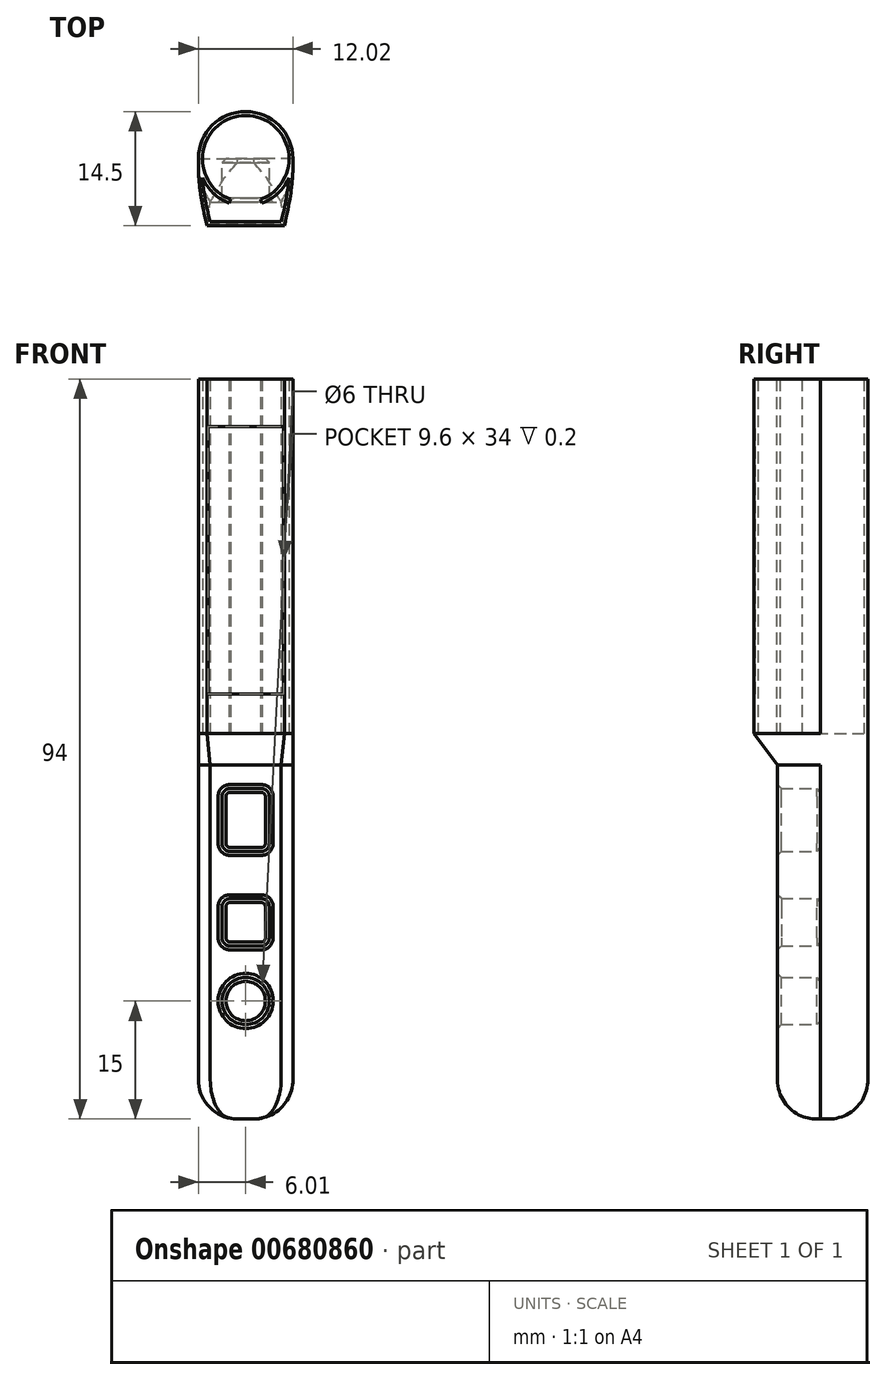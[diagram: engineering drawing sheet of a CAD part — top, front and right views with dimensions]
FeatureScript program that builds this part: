
annotation { "Feature Type Name" : "Feature", "Feature Type Description" : "" }
export const myFeature = defineFeature(function(context is Context, id is Id, definition is map)
    precondition{}
    {
        {
            var Q0;
            Q0=qCreatedBy(makeId("Top.planeOp"),FACE);
            var sketch = newSketch(context, id + "F0", { "sketchPlane" : qUnion([Q0])});
            skArc(sketch, "E0", {"start": v(1.91, -5.16) * mm, "mid": v(5.41, 0.97) * mm, "end": v(0, 5.5) * mm});
            skLineSegment(sketch, "E1.bottom", {"start": v(-5.5, 0) * mm, "end": v(5.5, 0) * mm});
            skLineSegment(sketch, "E1.top", {"start": v(-4.5, -8) * mm, "end": v(4.5, -8) * mm});
            skLineSegment(sketch, "E2.bottom", {"start": v(-6, 0) * mm, "end": v(6, 0) * mm});
            skLineSegment(sketch, "E2.top", {"start": v(-4.91, -8.5) * mm, "end": v(4.91, -8.5) * mm});
            skLineSegment(sketch, "E3.right", {"start": v(-2.09, -5.62) * mm, "end": v(-1.91, -5.16) * mm});
            skPoint(sketch, "E3.middle", {"position": v(0, -6) * mm});
            skArc(sketch, "E4.trimOffspring", {"start": v(-5.5, -2.4) * mm, "mid": v(-4.12, -4.36) * mm, "end": v(-2.09, -5.62) * mm});
            skArc(sketch, "E5.trimOffspring", {"start": v(6, 0) * mm, "mid": v(0, 6) * mm, "end": v(-6, 0) * mm});
            skLineSegment(sketch, "E6", {"start": v(4.5, -8) * mm, "end": v(-4.5, -8) * mm});
            skFitSpline(sketch, "E7", {"points": [v(-6, 0) * mm, v(-4.91, -8.5) * mm], "startDerivative": vector(-0.16, -5.74) * mm, "endDerivative": vector(3.03, -12.46) * mm});
            skFitSpline(sketch, "E8", {"points": [v(-5.5, -2.4) * mm, v(-4.5, -8) * mm], "startDerivative": vector(0.65, -6.73) * mm, "endDerivative": vector(1.57, -6.04) * mm});
            skPoint(sketch, "E9.MirrorCS.end.orphan", {"position": v(4.91, -8.5) * mm});
            skPoint(sketch, "E9.MirrorCS.start.orphan", {"position": v(6, 0) * mm});
            skPoint(sketch, "E10.MirrorCS.end.orphan", {"position": v(4.5, -8) * mm});
            skPoint(sketch, "E10.MirrorCS.start.orphan", {"position": v(5.5, -2.4) * mm});
            skFitSpline(sketch, "E11.MirrorCS", {"points": [v(6, 0) * mm, v(4.91, -8.5) * mm], "startDerivative": vector(0.16, -5.74) * mm, "endDerivative": vector(-3.03, -12.46) * mm});
            skFitSpline(sketch, "E12.MirrorCS", {"points": [v(5.5, -2.4) * mm, v(4.5, -8) * mm], "startDerivative": vector(-0.65, -6.73) * mm, "endDerivative": vector(-1.57, -6.04) * mm});
            skArc(sketch, "E13.MirrorCS", {"start": v(5.5, -2.4) * mm, "mid": v(4.12, -4.36) * mm, "end": v(2.09, -5.62) * mm});
            skLineSegment(sketch, "E14.MirrorCS", {"start": v(2.09, -5.62) * mm, "end": v(1.91, -5.16) * mm});
            skArc(sketch, "E15", {"start": v(0, 5.5) * mm, "mid": v(-5.41, 0.97) * mm, "end": v(-1.91, -5.16) * mm});
            skSolve(sketch);
        }
        {
            var Q0;
            Q0 = qSketchRegion(id + "F0", true);
            extrude(context, id + "F1", {"entities" : qUnion([Q0]), "depth" : 45 * mm, "offsetDistance" : 25.4 * mm});
        }
        {
            var Q0;
            Q0=makeQuery(id+"F1.opExtrude","SWEPT_FACE",FACE,{"disambiguationData":[OSD([sQuery(id+"F0.wireOp",EDGE,"E2.top")])]});
            var sketch = newSketch(context, id + "F2", { "sketchPlane" : qUnion([Q0])});
            skLineSegment(sketch, "E16.bottom", {"start": v(-4.91, 5) * mm, "end": v(4.8, 5) * mm});
            skLineSegment(sketch, "E16.top", {"start": v(-4.8, 39) * mm, "end": v(4.91, 39) * mm});
            skLineSegment(sketch, "E16.left", {"start": v(-4.8, 5) * mm, "end": v(-4.8, 39) * mm});
            skLineSegment(sketch, "E16.right", {"start": v(4.8, 5) * mm, "end": v(4.8, 39) * mm});
            skPoint(sketch, "E16.middle", {"position": v(0, 22) * mm});
            skSolve(sketch);
        }
        {
            var Q0;
            Q0=qCreatedBy(makeId("Top.planeOp"),FACE);
            cPlane(context, id + "F3", {"entities" : qUnion([Q0]), "cplaneType" : CPlaneType.OFFSET, "offset" : 4 * mm, "oppositeDirection" : true, "width" : 150 * mm, "height" : 150 * mm});
        }
        {
            var Q0;
            {var subQ2=sQuery(id+"F2.wireOp",EDGE,"E16.left");Q0=makeQuery(id+"F2.imprint","IMPRINT",FACE,{"disambiguationData":[TD([[makeQuery(id+"F2.imprint","IMPRINT",EDGE,{"derivedFrom":subQ2}),-1.0]])]});}
            extrude(context, id + "F4", {"entities" : qUnion([Q0]), "operationType" : NewBodyOperationType.REMOVE, "depth" : -0.2 * mm, "offsetDistance" : 25 * mm});
        }
        {
            var Q0;
            Q0=qCreatedBy(makeId("Top.planeOp"),FACE);
            var sketch = newSketch(context, id + "F5", { "sketchPlane" : qUnion([Q0])});
            skArc(sketch, "E17", {"start": v(6, 0) * mm, "mid": v(0, 6) * mm, "end": v(-6, 0) * mm});
            skLineSegment(sketch, "E18", {"start": v(-4.91, -8.5) * mm, "end": v(4.91, -8.5) * mm});
            skFitSpline(sketch, "E19", {"points": [v(-6, 0) * mm, v(-4.91, -8.5) * mm], "startDerivative": vector(0.05, -13.63) * mm, "endDerivative": vector(1.73, -8.34) * mm});
            skFitSpline(sketch, "E20.MirrorCS", {"points": [v(6, 0) * mm, v(4.91, -8.5) * mm], "startDerivative": vector(-0.05, -13.63) * mm, "endDerivative": vector(-1.73, -8.34) * mm});
            skSolve(sketch);
        }
        {
            var Q0;
            Q0=qCreatedBy(id+"F3.planeOp",FACE);
            var sketch = newSketch(context, id + "F6", { "sketchPlane" : qUnion([Q0])});
            skArc(sketch, "E21", {"start": v(6, 0) * mm, "mid": v(0, 6) * mm, "end": v(-6, 0) * mm});
            skLineSegment(sketch, "E22", {"start": v(-4.5, -5.5) * mm, "end": v(4.5, -5.5) * mm});
            skFitSpline(sketch, "E23", {"points": [v(-6, 0) * mm, v(-4.5, -5.5) * mm], "startDerivative": vector(-0.15, -9.4) * mm, "endDerivative": vector(2.63, -4.6) * mm});
            skFitSpline(sketch, "E24.MirrorCS", {"points": [v(6, 0) * mm, v(4.5, -5.5) * mm], "startDerivative": vector(0.15, -9.4) * mm, "endDerivative": vector(-2.63, -4.6) * mm});
            skPoint(sketch, "E25", {"position": v(0, -5.5) * mm});
            skSolve(sketch);
        }
        {
            var Q0;
            Q0=qCreatedBy(makeId("Right.planeOp"),FACE);
            var sketch = newSketch(context, id + "F7", { "sketchPlane" : qUnion([Q0])});
            skFitSpline(sketch, "E26", {"points": [v(-8.5, 0) * mm, v(-5.5, -4) * mm], "startDerivative": vector(-0.11, -4.2) * mm, "endDerivative": vector(0.02, -5.23) * mm});
            skLineSegment(sketch, "E27", {"start": v(6, 0) * mm, "end": v(6, -4) * mm});
            skSolve(sketch);
        }
        {
            var Q1;
            Q1=makeQuery(id+"F5.imprint","IMPRINT",FACE,{"disambiguationData":[TD([[makeQuery(id+"F5.imprint","IMPRINT",EDGE,{"derivedFrom":sQuery(id+"F5.wireOp",EDGE,"E17")}),1.0]])]});
            var Q2;
            Q2=makeQuery(id+"F6.imprint","IMPRINT",FACE,{"disambiguationData":[TD([[makeQuery(id+"F6.imprint","IMPRINT",EDGE,{"derivedFrom":sQuery(id+"F6.wireOp",EDGE,"E21")}),1.0]])]});
            var Q3;
            Q3=sQuery(id+"F7.wireOp",EDGE,"E26");
            loft(context, id + "F8", {"operationType" : NewBodyOperationType.ADD, "sheetProfilesArray" : [{ "sheetProfileEntities" : qUnion([Q1]) }, { "sheetProfileEntities" : qUnion([Q2]) }], "guidesArray" : [{ "guideEntities" : qUnion([Q3]), "guideDerivativeType" : LoftGuideDerivativeType.DEFAULT, "guideDerivativeMagnitude" : 1 }]});
        }
        {
            var Q0;
            Q0=makeQuery(id+"F6.imprint","IMPRINT",FACE,{"disambiguationData":[TD([[makeQuery(id+"F6.imprint","IMPRINT",EDGE,{"derivedFrom":sQuery(id+"F6.wireOp",EDGE,"E21")}),1.0]])]});
            extrude(context, id + "F9", {"entities" : qUnion([Q0]), "operationType" : NewBodyOperationType.ADD, "oppositeDirection" : true, "depth" : 45 * mm, "offsetDistance" : 25 * mm});
        }
        {
            var Q0;
            Q0=makeQuery(id+"F9.opExtrude","CAP_FACE",FACE,{"disambiguationData":[OSD([sQuery(id+"F6.wireOp",EDGE,"E21"),sQuery(id+"F6.wireOp",EDGE,"E22"),sQuery(id+"F6.wireOp",EDGE,"E23"),sQuery(id+"F6.wireOp",EDGE,"E24.MirrorCS")])],"isStart":false});
            fillet(context, id + "F10", {"entities" : qUnion([Q0]), "radius" : 5 * mm, "tangentPropagation" : true, "allowEdgeOverflow" : false});
        }
        {
            var Q0;
            Q0=qCreatedBy(makeId("Front.planeOp"),FACE);
            var sketch = newSketch(context, id + "F11", { "sketchPlane" : qUnion([Q0])});
            skLineSegment(sketch, "E28.bottom", {"start": v(-2, -7) * mm, "end": v(2, -7) * mm});
            skLineSegment(sketch, "E28.top", {"start": v(-2, -15) * mm, "end": v(2, -15) * mm});
            skLineSegment(sketch, "E28.left", {"start": v(-3, -8) * mm, "end": v(-3, -14) * mm});
            skLineSegment(sketch, "E28.right", {"start": v(3, -8) * mm, "end": v(3, -14) * mm});
            skLineSegment(sketch, "E29.bottom", {"start": v(-2, -21) * mm, "end": v(2, -21) * mm});
            skLineSegment(sketch, "E29.top", {"start": v(-2, -27) * mm, "end": v(2, -27) * mm});
            skLineSegment(sketch, "E29.left", {"start": v(-3, -22) * mm, "end": v(-3, -26) * mm});
            skLineSegment(sketch, "E29.right", {"start": v(3, -22) * mm, "end": v(3, -26) * mm});
            skCircle(sketch, "E30", {"center": v(0, -34) * mm, "radius": 3 * mm});
            skPoint(sketch, "E31.visualSharp", {"position": v(3, -7) * mm});
            skArc(sketch, "E31.filletArc", {"start": v(3, -8) * mm, "mid": v(2.7, -7.3) * mm, "end": v(2, -7) * mm});
            skPoint(sketch, "E32.visualSharp", {"position": v(-3, -15) * mm});
            skArc(sketch, "E32.filletArc", {"start": v(-3, -14) * mm, "mid": v(-2.7, -14.7) * mm, "end": v(-2, -15) * mm});
            skPoint(sketch, "E33.visualSharp", {"position": v(3, -15) * mm});
            skArc(sketch, "E33.filletArc", {"start": v(2, -15) * mm, "mid": v(2.7, -14.7) * mm, "end": v(3, -14) * mm});
            skPoint(sketch, "E34.visualSharp", {"position": v(-3, -7) * mm});
            skArc(sketch, "E34.filletArc", {"start": v(-2, -7) * mm, "mid": v(-2.7, -7.3) * mm, "end": v(-3, -8) * mm});
            skPoint(sketch, "E35.visualSharp", {"position": v(-3, -21) * mm});
            skArc(sketch, "E35.filletArc", {"start": v(-2, -21) * mm, "mid": v(-2.7, -21.3) * mm, "end": v(-3, -22) * mm});
            skPoint(sketch, "E36.visualSharp", {"position": v(3, -21) * mm});
            skArc(sketch, "E36.filletArc", {"start": v(3, -22) * mm, "mid": v(2.7, -21.3) * mm, "end": v(2, -21) * mm});
            skPoint(sketch, "E37.visualSharp", {"position": v(-3, -27) * mm});
            skArc(sketch, "E37.filletArc", {"start": v(-3, -26) * mm, "mid": v(-2.7, -26.7) * mm, "end": v(-2, -27) * mm});
            skPoint(sketch, "E38.visualSharp", {"position": v(3, -27) * mm});
            skArc(sketch, "E38.filletArc", {"start": v(2, -27) * mm, "mid": v(2.7, -26.7) * mm, "end": v(3, -26) * mm});
            skSolve(sketch);
        }
        {
            var Q0;
            Q0 = qSketchRegion(id + "F11", true);
            extrude(context, id + "F12", {"entities" : qUnion([Q0]), "operationType" : NewBodyOperationType.REMOVE, "depth" : 10 * mm, "offsetDistance" : 25 * mm});
        }
        {
            var Q0;
            Q0=makeQuery(id+"F12.boolean.opBoolean","COPY",FACE,{"derivedFrom":makeQuery(id+"F12.opExtrude","SWEPT_FACE",FACE,{"disambiguationData":[OSD([sQuery(id+"F11.wireOp",EDGE,"E28.right")])]})});
            var Q1;
            Q1=makeQuery(id+"F12.boolean.opBoolean","COPY",FACE,{"derivedFrom":makeQuery(id+"F12.opExtrude","SWEPT_FACE",FACE,{"disambiguationData":[OSD([sQuery(id+"F11.wireOp",EDGE,"E28.bottom")])]})});
            var Q2;
            Q2=makeQuery(id+"F12.boolean.opBoolean","COPY",FACE,{"derivedFrom":makeQuery(id+"F12.opExtrude","SWEPT_FACE",FACE,{"disambiguationData":[OSD([sQuery(id+"F11.wireOp",EDGE,"E29.bottom")])]})});
            var Q3;
            Q3=makeQuery(id+"F12.boolean.opBoolean","COPY",FACE,{"derivedFrom":makeQuery(id+"F12.opExtrude","SWEPT_FACE",FACE,{"disambiguationData":[OSD([sQuery(id+"F11.wireOp",EDGE,"E29.right")])]})});
            var Q4;
            Q4=makeQuery(id+"F12.boolean.opBoolean","COPY",FACE,{"derivedFrom":makeQuery(id+"F12.opExtrude","SWEPT_FACE",FACE,{"disambiguationData":[OSD([sQuery(id+"F11.wireOp",EDGE,"E30")])]})});
            var Q5;
            Q5=makeQuery(id+"F12.boolean.opBoolean","COPY",FACE,{"derivedFrom":makeQuery(id+"F12.opExtrude","SWEPT_FACE",FACE,{"disambiguationData":[OSD([sQuery(id+"F11.wireOp",EDGE,"E29.top")])]})});
            var Q6;
            Q6=makeQuery(id+"F12.boolean.opBoolean","COPY",FACE,{"derivedFrom":makeQuery(id+"F12.opExtrude","SWEPT_FACE",FACE,{"disambiguationData":[OSD([sQuery(id+"F11.wireOp",EDGE,"E29.left")])]})});
            var Q7;
            Q7=makeQuery(id+"F12.boolean.opBoolean","COPY",FACE,{"derivedFrom":makeQuery(id+"F12.opExtrude","SWEPT_FACE",FACE,{"disambiguationData":[OSD([sQuery(id+"F11.wireOp",EDGE,"E28.top")])]})});
            var Q8;
            Q8=makeQuery(id+"F12.boolean.opBoolean","COPY",FACE,{"derivedFrom":makeQuery(id+"F12.opExtrude","SWEPT_FACE",FACE,{"disambiguationData":[OSD([sQuery(id+"F11.wireOp",EDGE,"E28.left")])]})});
            chamfer(context, id + "F13", {"entities" : qUnion([Q0, Q1, Q2, Q3, Q4, Q5, Q6, Q7, Q8]), "width" : 0.5 * mm, "tangentPropagation" : true});
        }
    });
